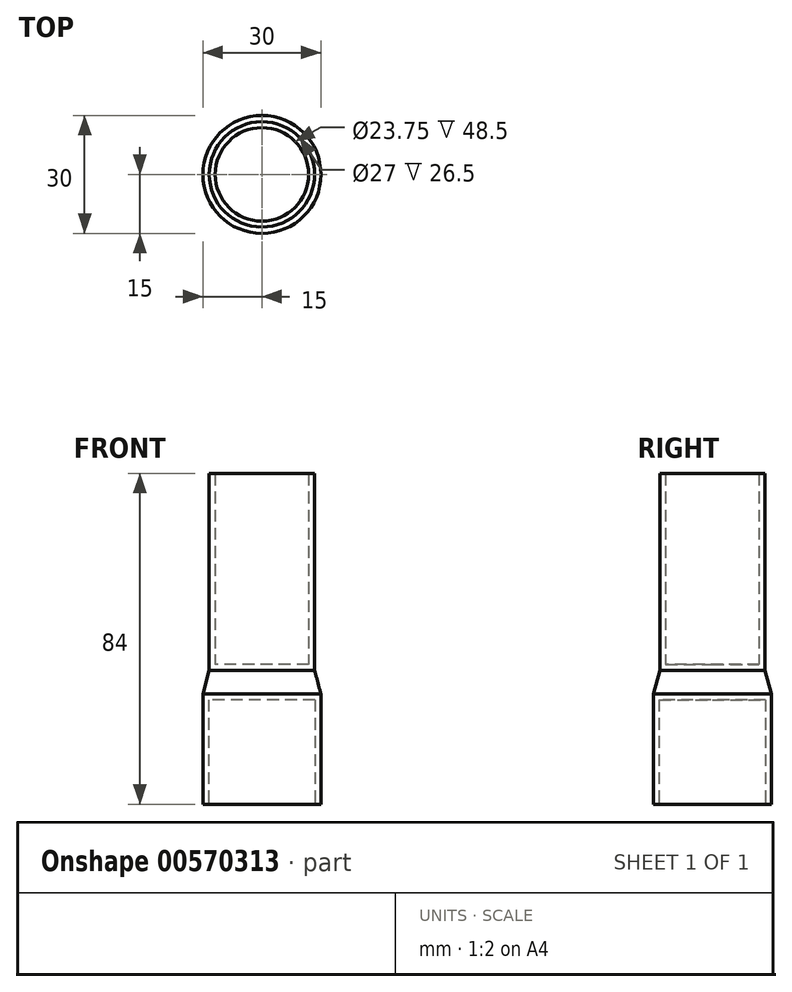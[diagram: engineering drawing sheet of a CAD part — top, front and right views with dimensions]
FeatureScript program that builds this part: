
annotation { "Feature Type Name" : "Feature", "Feature Type Description" : "" }
export const myFeature = defineFeature(function(context is Context, id is Id, definition is map)
    precondition{}
    {
        {
            var Q0;
            Q0=qCreatedBy(makeId("Top.planeOp"),FACE);
            var sketch = newSketch(context, id + "F0", { "sketchPlane" : qUnion([Q0])});
            skCircle(sketch, "E0", {"center": v(0, 0) * mm, "radius": 15 * mm});
            skCircle(sketch, "E1", {"center": v(0, 0) * mm, "radius": 13.5 * mm});
            skSolve(sketch);
        }
        {
            var Q0;
            Q0=makeQuery(id+"F0.imprint","IMPRINT",FACE,{"disambiguationData":[TD([[makeQuery(id+"F0.imprint","IMPRINT",EDGE,{"derivedFrom":sQuery(id+"F0.wireOp",EDGE,"E0")}),1.0]])]});
            var Q1;
            Q1=makeQuery(id+"F0.imprint","IMPRINT",FACE,{"disambiguationData":[TD([[makeQuery(id+"F0.imprint","IMPRINT",EDGE,{"derivedFrom":sQuery(id+"F0.wireOp",EDGE,"E1")}),1.0]])]});
            extrude(context, id + "F1", {"entities" : qUnion([Q0, Q1]), "depth" : 28 * mm, "offsetDistance" : 25 * mm});
        }
        {
            var Q0;
            Q0=qCreatedBy(makeId("Top.planeOp"),FACE);
            var sketch = newSketch(context, id + "F2", { "sketchPlane" : qUnion([Q0])});
            skCircle(sketch, "E2", {"center": v(0, 0) * mm, "radius": 13.38 * mm});
            skCircle(sketch, "E3", {"center": v(0, 0) * mm, "radius": 11.88 * mm});
            skSolve(sketch);
        }
        {
            var Q0;
            Q0=makeQuery(id+"F2.imprint","IMPRINT",FACE,{"disambiguationData":[TD([[makeQuery(id+"F2.imprint","IMPRINT",EDGE,{"derivedFrom":sQuery(id+"F2.wireOp",EDGE,"E2")}),1.0]])]});
            var Q1;
            Q1=makeQuery(id+"F2.imprint","IMPRINT",FACE,{"disambiguationData":[TD([[makeQuery(id+"F2.imprint","IMPRINT",EDGE,{"derivedFrom":sQuery(id+"F2.wireOp",EDGE,"E3")}),1.0]])]});
            extrude(context, id + "F3", {"entities" : qUnion([Q0, Q1]), "depth" : 50 * mm, "offsetDistance" : 25 * mm});
        }
        {
            var Q0;
            Q0=makeQuery(id+"F3.opExtrude","SWEPT_BODY",BODY,{"disambiguationData":[OSD([sQuery(id+"F2.wireOp",EDGE,"E2"),sQuery(id+"F2.wireOp",EDGE,"E3")])]});
            transform(context, id + "F4", {"entities" : qUnion([Q0]), "transformType" : TransformType.TRANSLATION_3D, "dx" : 0 * mm, "dy" : 0 * mm, "dz" : 34 * mm, "makeCopy" : false});
        }
        {
            var Q0;
            Q0=makeQuery(id+"F1.opExtrude","CAP_FACE",FACE,{"disambiguationData":[OSD([sQuery(id+"F0.wireOp",EDGE,"E0")])],"isStart":false});
            var Q1;
            Q1=makeQuery(id+"F3.opExtrude","CAP_FACE",FACE,{"disambiguationData":[OSD([sQuery(id+"F2.wireOp",EDGE,"E2")])],"isStart":true});
            extrude(context, id + "F5", {"entities" : qUnion([Q0]), "endBound" : BoundingType.UP_TO_SURFACE, "depth" : 25 * mm, "endBoundEntityFace" : qUnion([Q1]), "offsetDistance" : 25 * mm});
        }
        {
            var Q0;
            Q0=makeQuery(id+"F5.opExtrude","CAP_EDGE",EDGE,{"disambiguationData":[OSD([sQuery(id+"F0.wireOp",EDGE,"E0")])],"isStart":false});
            chamfer(context, id + "F6", {"entities" : qUnion([Q0]), "chamferType" : ChamferType.TWO_OFFSETS, "width1" : 1.62 * mm, "oppositeDirection" : false, "width2" : 6 * mm, "tangentPropagation" : true});
        }
        {
            var Q0;
            Q0=makeQuery(id+"F3.opExtrude","CAP_FACE",FACE,{"disambiguationData":[OSD([sQuery(id+"F2.wireOp",EDGE,"E2")])],"isStart":false});
            var Q1;
            Q1=makeQuery(id+"F1.opExtrude","CAP_FACE",FACE,{"disambiguationData":[OSD([sQuery(id+"F0.wireOp",EDGE,"E0")])],"isStart":true});
            var Q2;
            Q2=makeQuery(id+"F1.opExtrude","SWEPT_BODY",BODY,{"disambiguationData":[OSD([sQuery(id+"F0.wireOp",EDGE,"E0")])]});
            shell(context, id + "F7", {"entities" : qUnion([Q0, Q1]), "parts" : qUnion([Q2]), "thickness" : 1.5 * mm});
        }
    });
